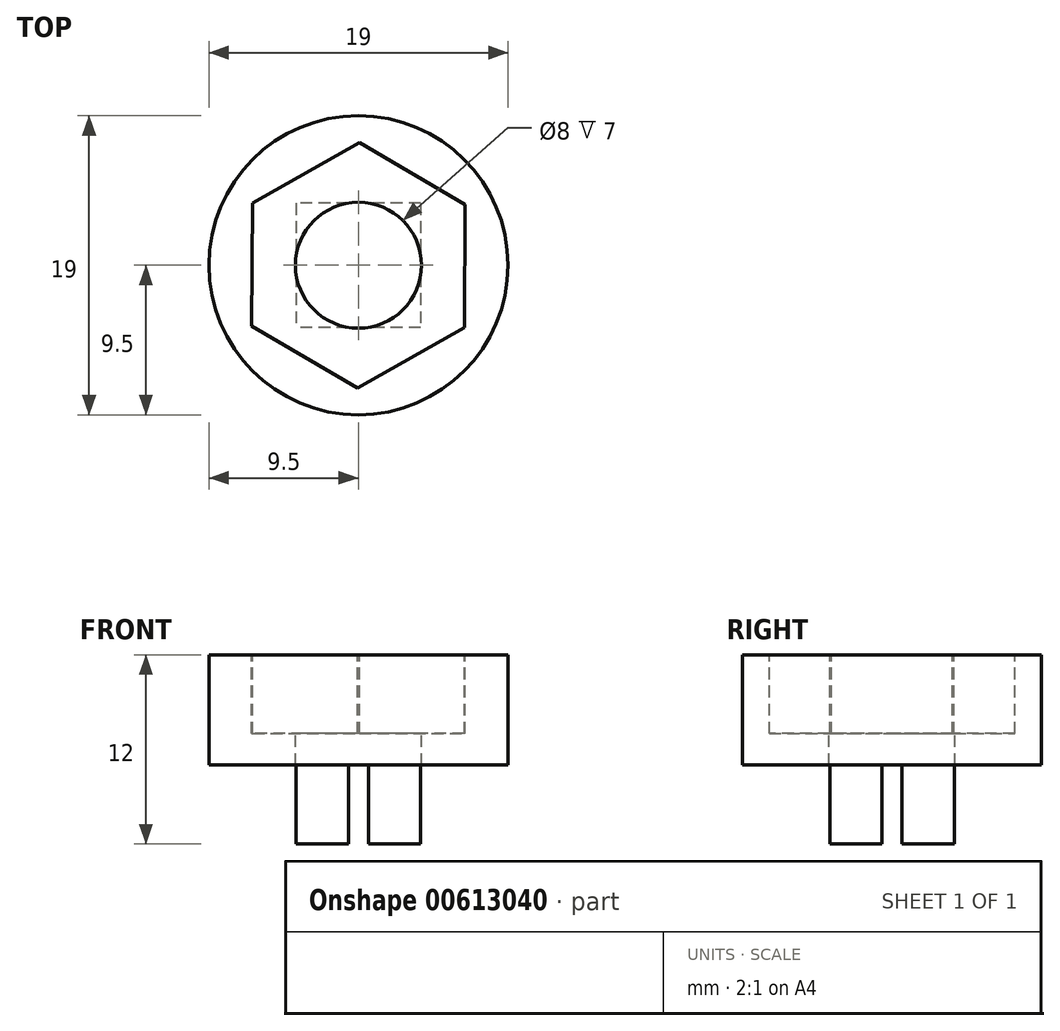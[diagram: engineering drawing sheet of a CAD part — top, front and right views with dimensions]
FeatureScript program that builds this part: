
annotation { "Feature Type Name" : "Feature", "Feature Type Description" : "" }
export const myFeature = defineFeature(function(context is Context, id is Id, definition is map)
    precondition{}
    {
        {
            var Q0;
            Q0=qCreatedBy(makeId("Top.planeOp"),FACE);
            var sketch = newSketch(context, id + "F0", { "sketchPlane" : qUnion([Q0])});
            skCircle(sketch, "E0", {"center": v(0, 0) * mm, "radius": 9.5 * mm});
            skSolve(sketch);
        }
        {
            var Q0;
            Q0=makeQuery(id+"F0.imprint","IMPRINT",FACE,{"disambiguationData":[TD([[makeQuery(id+"F0.imprint","IMPRINT",EDGE,{"derivedFrom":sQuery(id+"F0.wireOp",EDGE,"E0")}),1.0]])]});
            extrude(context, id + "F1", {"entities" : qUnion([Q0]), "depth" : 7 * mm, "offsetDistance" : 25 * mm});
        }
        {
            var Q0;
            Q0=makeQuery(id+"F1.opExtrude","CAP_FACE",FACE,{"disambiguationData":[OSD([sQuery(id+"F0.wireOp",EDGE,"E0")])],"isStart":false});
            var sketch = newSketch(context, id + "F2", { "sketchPlane" : qUnion([Q0])});
            skCircle(sketch, "E1.cCircle", {"center": v(0, 0) * mm, "radius": 6.75 * mm, "construction": true});
            skLineSegment(sketch, "E1.0", {"start": v(6.72, -3.94) * mm, "end": v(-0.05, -7.8) * mm});
            skLineSegment(sketch, "E1.1", {"start": v(-0.05, -7.8) * mm, "end": v(-6.78, -3.85) * mm});
            skLineSegment(sketch, "E1.2", {"start": v(-6.78, -3.85) * mm, "end": v(-6.72, 3.94) * mm});
            skLineSegment(sketch, "E1.3", {"start": v(-6.72, 3.94) * mm, "end": v(0.05, 7.8) * mm});
            skLineSegment(sketch, "E1.4", {"start": v(0.05, 7.8) * mm, "end": v(6.78, 3.85) * mm});
            skLineSegment(sketch, "E1.5", {"start": v(6.78, 3.85) * mm, "end": v(6.72, -3.94) * mm});
            skPoint(sketch, "E1.0.midPoint", {"position": v(3.33, -5.87) * mm});
            skSolve(sketch);
        }
        {
            var Q0;
            Q0=makeQuery(id+"F2.imprint","IMPRINT",FACE,{"disambiguationData":[TD([[makeQuery(id+"F2.imprint","IMPRINT",EDGE,{"derivedFrom":sQuery(id+"F2.wireOp",EDGE,"E1.0")}),-1.0]])]});
            extrude(context, id + "F3", {"entities" : qUnion([Q0]), "operationType" : NewBodyOperationType.REMOVE, "oppositeDirection" : true, "depth" : 5 * mm, "offsetDistance" : 25 * mm});
        }
        {
            var Q0;
            Q0=makeQuery(id+"F1.opExtrude","CAP_FACE",FACE,{"disambiguationData":[OSD([sQuery(id+"F0.wireOp",EDGE,"E0")])],"isStart":true});
            var sketch = newSketch(context, id + "F4", { "sketchPlane" : qUnion([Q0])});
            skLineSegment(sketch, "E2.bottom", {"start": v(3.95, -3.95) * mm, "end": v(-3.95, -3.95) * mm});
            skLineSegment(sketch, "E2.top", {"start": v(3.95, 3.95) * mm, "end": v(-3.95, 3.95) * mm});
            skLineSegment(sketch, "E2.left", {"start": v(3.95, -3.95) * mm, "end": v(3.95, 3.95) * mm});
            skLineSegment(sketch, "E2.right", {"start": v(-3.95, -3.95) * mm, "end": v(-3.95, 3.95) * mm});
            skPoint(sketch, "E2.middle", {"position": v(0, 0) * mm});
            skSolve(sketch);
        }
        {
            var Q0;
            Q0=makeQuery(id+"F4.imprint","IMPRINT",FACE,{"disambiguationData":[TD([[makeQuery(id+"F4.imprint","IMPRINT",EDGE,{"derivedFrom":sQuery(id+"F4.wireOp",EDGE,"E2.bottom")}),-1.0]])]});
            extrude(context, id + "F5", {"entities" : qUnion([Q0]), "operationType" : NewBodyOperationType.ADD, "depth" : 5 * mm, "offsetDistance" : 25 * mm});
        }
        {
            var Q0;
            Q0=makeQuery(id+"F3.boolean.opBoolean","COPY",FACE,{"derivedFrom":makeQuery(id+"F3.opExtrude","CAP_FACE",FACE,{"disambiguationData":[OSD([sQuery(id+"F2.wireOp",EDGE,"E1.0"),sQuery(id+"F2.wireOp",EDGE,"E1.1"),sQuery(id+"F2.wireOp",EDGE,"E1.2"),sQuery(id+"F2.wireOp",EDGE,"E1.3"),sQuery(id+"F2.wireOp",EDGE,"E1.4"),sQuery(id+"F2.wireOp",EDGE,"E1.5")])],"isStart":false})});
            var sketch = newSketch(context, id + "F6", { "sketchPlane" : qUnion([Q0])});
            skCircle(sketch, "E3", {"center": v(0, 0) * mm, "radius": 4 * mm});
            skSolve(sketch);
        }
        {
            var Q0;
            Q0=makeQuery(id+"F6.imprint","IMPRINT",FACE,{"disambiguationData":[TD([[makeQuery(id+"F6.imprint","IMPRINT",EDGE,{"derivedFrom":sQuery(id+"F6.wireOp",EDGE,"E3")}),1.0]])]});
            extrude(context, id + "F7", {"entities" : qUnion([Q0]), "operationType" : NewBodyOperationType.REMOVE, "endBound" : BoundingType.THROUGH_ALL, "oppositeDirection" : true, "depth" : 25 * mm, "offsetDistance" : 25 * mm});
        }
    });
